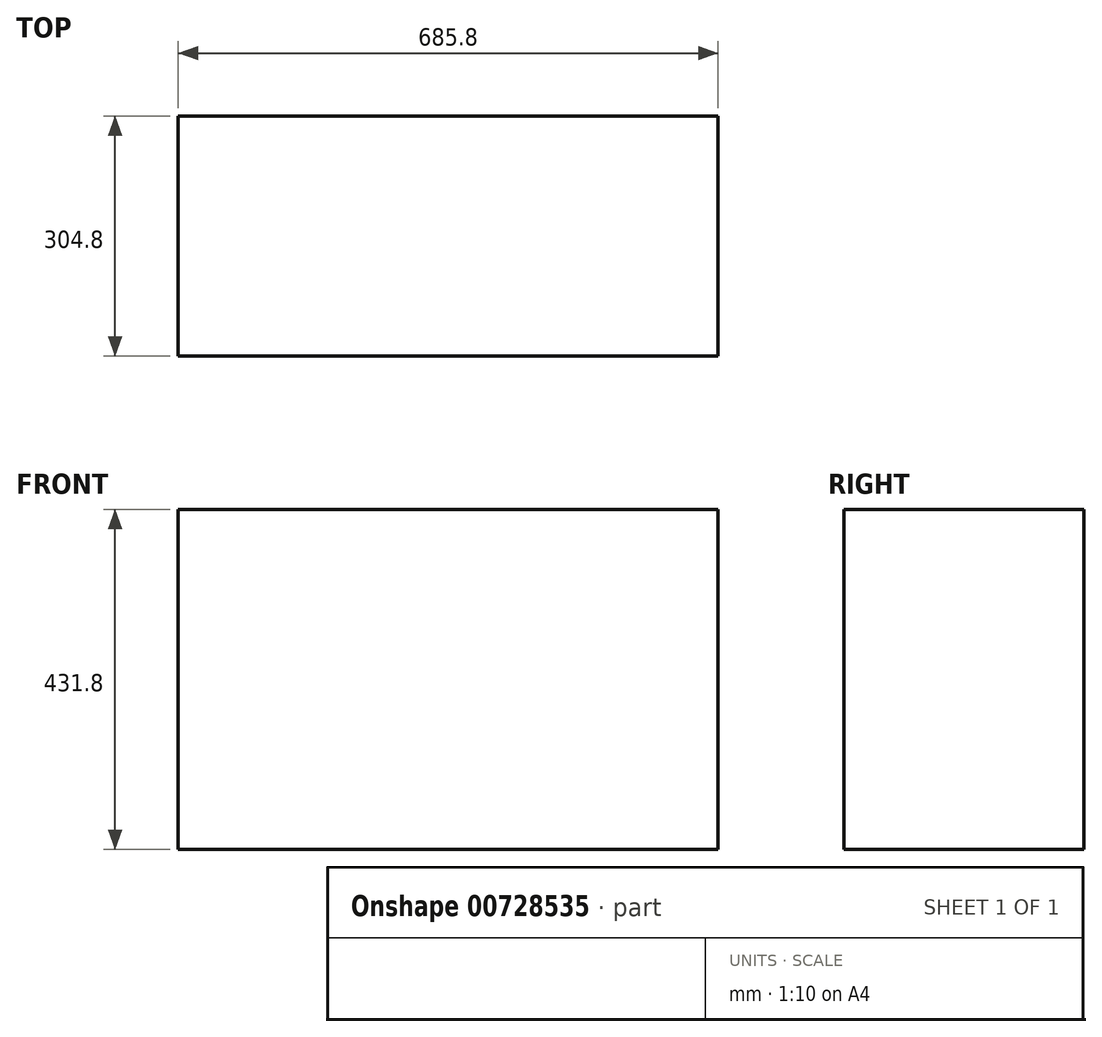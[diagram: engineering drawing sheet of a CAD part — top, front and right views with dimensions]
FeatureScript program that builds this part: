
annotation { "Feature Type Name" : "Feature", "Feature Type Description" : "" }
export const myFeature = defineFeature(function(context is Context, id is Id, definition is map)
    precondition{}
    {
        {
            var Q0;
            Q0=qCreatedBy(makeId("Top.planeOp"),FACE);
            var sketch = newSketch(context, id + "F0", { "sketchPlane" : qUnion([Q0])});
            skLineSegment(sketch, "E0.bottom", {"start": v(342.9, 152.4) * mm, "end": v(-342.9, 152.4) * mm});
            skLineSegment(sketch, "E0.top", {"start": v(342.9, -152.4) * mm, "end": v(-342.9, -152.4) * mm});
            skLineSegment(sketch, "E0.left", {"start": v(342.9, 152.4) * mm, "end": v(342.9, -152.4) * mm});
            skLineSegment(sketch, "E0.right", {"start": v(-342.9, 152.4) * mm, "end": v(-342.9, -152.4) * mm});
            skPoint(sketch, "E0.middle", {"position": v(0, 0) * mm});
            skSolve(sketch);
        }
        {
            var Q0;
            Q0 = qSketchRegion(id + "F0", true);
            extrude(context, id + "F1", {"entities" : qUnion([Q0]), "depth" : 431.8 * mm, "offsetDistance" : 25.4 * mm});
        }
    });
